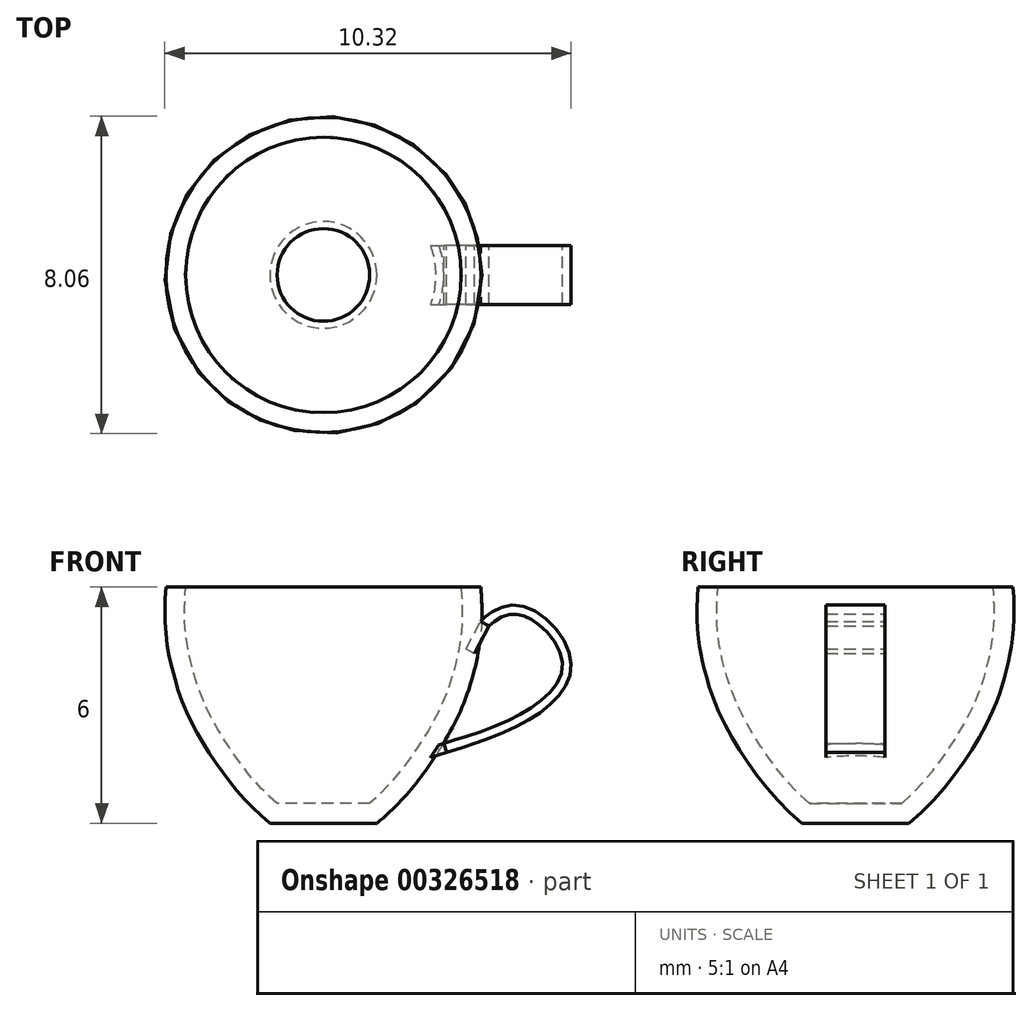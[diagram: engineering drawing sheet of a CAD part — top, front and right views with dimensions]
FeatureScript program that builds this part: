
annotation { "Feature Type Name" : "Feature", "Feature Type Description" : "" }
export const myFeature = defineFeature(function(context is Context, id is Id, definition is map)
    precondition{}
    {
        {
            var Q0;
            Q0=qCreatedBy(makeId("Front.planeOp"),FACE);
            var sketch = newSketch(context, id + "F0", { "sketchPlane" : qUnion([Q0])});
            skLineSegment(sketch, "E0", {"start": v(4, 6) * mm, "end": v(0, 6) * mm});
            skPoint(sketch, "E1.visualSharp", {"position": v(6, 33.92) * mm});
            skLineSegment(sketch, "E2", {"start": v(0, 6) * mm, "end": v(0, 0) * mm});
            skFitSpline(sketch, "E3", {"points": [v(4, 6) * mm, v(4, 4.8) * mm, v(3.6, 3.14) * mm, v(2.8, 1.65) * mm, v(1.36, 0) * mm], "startDerivative": vector(0.4, -5.45) * mm, "endDerivative": vector(-6.64, -5.34) * mm});
            skFitSpline(sketch, "E4", {"points": [v(1.36, 0) * mm, v(0, 0) * mm], "startDerivative": vector(-1.36, 0) * mm, "endDerivative": vector(-1.36, 0) * mm});
            skSolve(sketch);
        }
        {
            var Q0;
            Q0 = qSketchRegion(id + "F0", true);
            var Q1;
            Q1=sQuery(id+"F0.wireOp",EDGE,"E2");
            revolve(context, id + "F1", {"entities" : qUnion([Q0]), "axis" : qUnion([Q1]), "revolveType" : RevolveType.FULL});
        }
        {
            var Q0;
            Q0=makeQuery(id+"F1.opRevolve","SWEPT_FACE",FACE,{"disambiguationData":[OSD([sQuery(id+"F0.wireOp",EDGE,"E0")])]});
            shell(context, id + "F2", {"entities" : qUnion([Q0]), "thickness" : 0.5 * mm});
        }
        {
            var Q0;
            Q0=qCreatedBy(makeId("Front.planeOp"),FACE);
            var sketch = newSketch(context, id + "F3", { "sketchPlane" : qUnion([Q0])});
            skFitSpline(sketch, "E5", {"points": [v(3.99, 5.12) * mm, v(4.91, 5.54) * mm, v(6.28, 4.2) * mm, v(5.51, 2.81) * mm, v(3.13, 1.8) * mm], "startDerivative": vector(1.76, 2.23) * mm, "endDerivative": vector(-8.6, -2.71) * mm});
            skFitSpline(sketch, "E6.0", {"points": [v(4.17, 4.97) * mm, v(4.18, 4.99) * mm, v(4.22, 5.03) * mm, v(4.35, 5.13) * mm, v(4.53, 5.24) * mm, v(4.73, 5.3) * mm, v(4.87, 5.31) * mm, v(5.03, 5.29) * mm, v(5.2, 5.22) * mm, v(5.38, 5.11) * mm, v(5.6, 4.92) * mm, v(5.86, 4.63) * mm, v(6.05, 4.24) * mm, v(6.07, 3.92) * mm, v(5.97, 3.62) * mm, v(5.75, 3.31) * mm, v(5.42, 3.03) * mm, v(5.03, 2.78) * mm, v(4.6, 2.57) * mm, v(3.95, 2.3) * mm, v(3.42, 2.14) * mm, v(3.06, 2.03) * mm]});
            skLineSegment(sketch, "E7", {"start": v(3.99, 5.12) * mm, "end": v(4.2, 5) * mm});
            skLineSegment(sketch, "E8", {"start": v(3.06, 2.03) * mm, "end": v(3.13, 1.8) * mm});
            skSolve(sketch);
        }
        {
            var Q0;
            Q0=makeQuery(id+"F3.imprint","IMPRINT",FACE,{"disambiguationData":[TD([[makeQuery(id+"F3.imprint","IMPRINT",EDGE,{"derivedFrom":sQuery(id+"F3.wireOp",EDGE,"E5")}),-1.0]])]});
            extrude(context, id + "F4", {"entities" : qUnion([Q0]), "endBound" : BoundingType.SYMMETRIC, "depth" : 1.5 * mm});
        }
        {
            var Q0;
            Q0=makeQuery(id+"F4.opExtrude","SWEPT_FACE",FACE,{"disambiguationData":[OSD([sQuery(id+"F3.wireOp",EDGE,"E8")])]});
            extrude(context, id + "F5", {"entities" : qUnion([Q0]), "endBound" : BoundingType.UP_TO_NEXT, "depth" : 25 * mm});
        }
        {
            var Q0;
            Q0=makeQuery(id+"F4.opExtrude","SWEPT_FACE",FACE,{"disambiguationData":[OSD([sQuery(id+"F3.wireOp",EDGE,"E7")])]});
            extrude(context, id + "F6", {"entities" : qUnion([Q0]), "depth" : 0.79 * mm});
        }
    });
